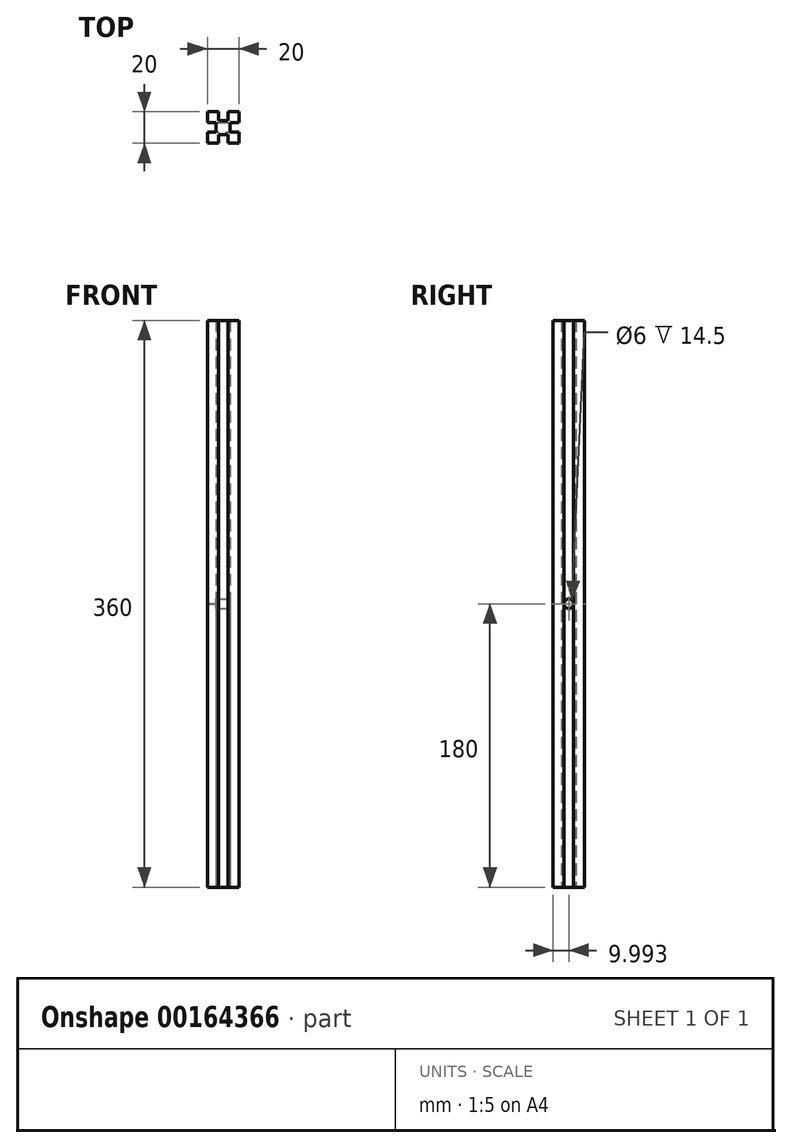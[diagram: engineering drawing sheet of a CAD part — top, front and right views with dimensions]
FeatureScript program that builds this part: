
annotation { "Feature Type Name" : "Feature", "Feature Type Description" : "" }
export const myFeature = defineFeature(function(context is Context, id is Id, definition is map)
    precondition{}
    {
        {
            var Q0;
            Q0=qCreatedBy(makeId("Top.planeOp"),FACE);
            var sketch = newSketch(context, id + "F0", { "sketchPlane" : qUnion([Q0])});
            skLineSegment(sketch, "E0.bottom", {"start": v(0, 0) * mm, "end": v(20, 0) * mm});
            skLineSegment(sketch, "E0.top", {"start": v(0, 20) * mm, "end": v(20, 20) * mm});
            skLineSegment(sketch, "E0.left", {"start": v(0, 0) * mm, "end": v(0, 20) * mm});
            skLineSegment(sketch, "E0.right", {"start": v(20, 0) * mm, "end": v(20, 20) * mm});
            skLineSegment(sketch, "E1.bottom", {"start": v(7, 20) * mm, "end": v(13, 20) * mm});
            skLineSegment(sketch, "E1.top", {"start": v(7, 14.5) * mm, "end": v(13, 14.5) * mm});
            skLineSegment(sketch, "E1.left", {"start": v(7, 20) * mm, "end": v(7, 14.5) * mm});
            skLineSegment(sketch, "E1.right", {"start": v(13, 20) * mm, "end": v(13, 14.5) * mm});
            skLineSegment(sketch, "E2.bottom", {"start": v(20, 13) * mm, "end": v(14.5, 13) * mm});
            skLineSegment(sketch, "E2.top", {"start": v(20, 7) * mm, "end": v(14.5, 7) * mm});
            skLineSegment(sketch, "E2.left", {"start": v(20, 13) * mm, "end": v(20, 7) * mm});
            skLineSegment(sketch, "E2.right", {"start": v(14.5, 13) * mm, "end": v(14.5, 7) * mm});
            skLineSegment(sketch, "E3.bottom", {"start": v(13, 0) * mm, "end": v(7, 0) * mm});
            skLineSegment(sketch, "E3.top", {"start": v(13, 5.5) * mm, "end": v(7, 5.5) * mm});
            skLineSegment(sketch, "E3.left", {"start": v(13, 0) * mm, "end": v(13, 5.5) * mm});
            skLineSegment(sketch, "E3.right", {"start": v(7, 0) * mm, "end": v(7, 5.5) * mm});
            skLineSegment(sketch, "E4.bottom", {"start": v(0, 7) * mm, "end": v(5.5, 7) * mm});
            skLineSegment(sketch, "E4.top", {"start": v(0, 13) * mm, "end": v(5.5, 13) * mm});
            skLineSegment(sketch, "E4.left", {"start": v(0, 7) * mm, "end": v(0, 13) * mm});
            skLineSegment(sketch, "E4.right", {"start": v(5.5, 7) * mm, "end": v(5.5, 13) * mm});
            skSolve(sketch);
        }
        {
            var Q0;
            Q0=makeQuery(id+"F0.imprint","IMPRINT",FACE,{"disambiguationData":[TD([[makeQuery(id+"F0.imprint","IMPRINT",EDGE,{"derivedFrom":sQuery(id+"F0.wireOp",EDGE,"E1.top")}),-1.0]])]});
            extrude(context, id + "F1", {"entities" : qUnion([Q0]), "depth" : 360 * mm});
        }
        {
            var Q0;
            Q0=makeQuery(id+"F1.opExtrude","SWEPT_FACE",FACE,{"disambiguationData":[OSD([sQuery(id+"F0.wireOp",EDGE,"E2.right")])]});
            var sketch = newSketch(context, id + "F2", { "sketchPlane" : qUnion([Q0])});
            skCircle(sketch, "E5", {"center": v(10, 180) * mm, "radius": 3 * mm});
            skPoint(sketch, "E5.centerSnap0", {"position": v(13, 180) * mm});
            skSolve(sketch);
        }
        {
            var Q0;
            Q0 = qSketchRegion(id + "F2", true);
            extrude(context, id + "F3", {"entities" : qUnion([Q0]), "operationType" : NewBodyOperationType.REMOVE, "oppositeDirection" : true, "depth" : 25 * mm});
        }
    });
